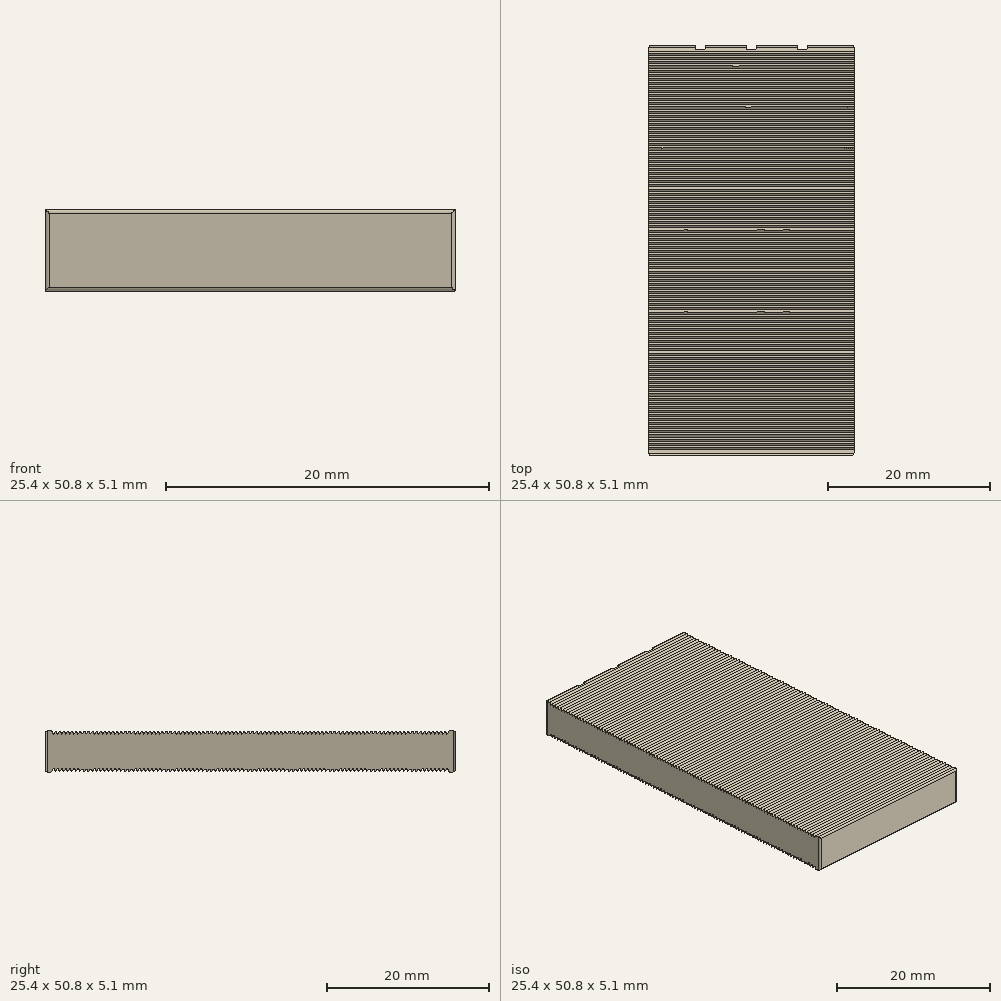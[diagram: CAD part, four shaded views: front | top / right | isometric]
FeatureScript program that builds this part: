
annotation { "Feature Type Name" : "Feature", "Feature Type Description" : "" }
export const myFeature = defineFeature(function(context is Context, id is Id, definition is map)
    precondition{}
    {
        {
            var Q0;
            Q0=qCreatedBy(makeId("Front.planeOp"),FACE);
            var sketch = newSketch(context, id + "F0", { "sketchPlane" : qUnion([Q0])});
            skLineSegment(sketch, "E0.bottom", {"start": v(12.7, -2.54) * mm, "end": v(-12.7, -2.54) * mm});
            skLineSegment(sketch, "E0.top", {"start": v(12.7, 2.54) * mm, "end": v(-12.7, 2.54) * mm});
            skLineSegment(sketch, "E0.left", {"start": v(12.7, -2.54) * mm, "end": v(12.7, 2.54) * mm});
            skLineSegment(sketch, "E0.right", {"start": v(-12.7, -2.54) * mm, "end": v(-12.7, 2.54) * mm});
            skPoint(sketch, "E0.middle", {"position": v(0, 0) * mm});
            skSolve(sketch);
        }
        {
            var Q0;
            Q0=qSketchRegion(id+"F0",true);
            extrude(context, id + "F1", {"entities" : qUnion([Q0]), "endBound" : BoundingType.SYMMETRIC, "depth" : 50.8 * mm, "offsetDistance" : 25.4 * mm});
        }
        {
            var Q0;
            Q0=qCreatedBy(makeId("Right.planeOp"),FACE);
            var sketch = newSketch(context, id + "F2", { "sketchPlane" : qUnion([Q0])});
            skLineSegment(sketch, "E1", {"start": v(0.25, -2.54) * mm, "end": v(0, -2.1) * mm});
            skLineSegment(sketch, "E2", {"start": v(0, -2.1) * mm, "end": v(-0.25, -2.54) * mm});
            skLineSegment(sketch, "E3.1.0.0", {"start": v(0.76, -2.54) * mm, "end": v(0.5, -2.1) * mm});
            skLineSegment(sketch, "E3.1.0.1", {"start": v(0.5, -2.1) * mm, "end": v(0.25, -2.54) * mm});
            skLineSegment(sketch, "E3.2.0.0", {"start": v(1.27, -2.54) * mm, "end": v(1.02, -2.1) * mm});
            skLineSegment(sketch, "E3.2.0.1", {"start": v(1.02, -2.1) * mm, "end": v(0.76, -2.54) * mm});
            skLineSegment(sketch, "E3.3.0.0", {"start": v(1.78, -2.54) * mm, "end": v(1.52, -2.1) * mm});
            skLineSegment(sketch, "E3.3.0.1", {"start": v(1.52, -2.1) * mm, "end": v(1.27, -2.54) * mm});
            skLineSegment(sketch, "E3.4.0.0", {"start": v(2.29, -2.54) * mm, "end": v(2.03, -2.1) * mm});
            skLineSegment(sketch, "E3.4.0.1", {"start": v(2.03, -2.1) * mm, "end": v(1.78, -2.54) * mm});
            skLineSegment(sketch, "E3.5.0.0", {"start": v(2.8, -2.54) * mm, "end": v(2.54, -2.1) * mm});
            skLineSegment(sketch, "E3.5.0.1", {"start": v(2.54, -2.1) * mm, "end": v(2.29, -2.54) * mm});
            skLineSegment(sketch, "E3.6.0.0", {"start": v(3.3, -2.54) * mm, "end": v(3.05, -2.1) * mm});
            skLineSegment(sketch, "E3.6.0.1", {"start": v(3.05, -2.1) * mm, "end": v(2.8, -2.54) * mm});
            skLineSegment(sketch, "E3.7.0.0", {"start": v(3.81, -2.54) * mm, "end": v(3.56, -2.1) * mm});
            skLineSegment(sketch, "E3.7.0.1", {"start": v(3.56, -2.1) * mm, "end": v(3.3, -2.54) * mm});
            skLineSegment(sketch, "E3.8.0.0", {"start": v(4.32, -2.54) * mm, "end": v(4.06, -2.1) * mm});
            skLineSegment(sketch, "E3.8.0.1", {"start": v(4.06, -2.1) * mm, "end": v(3.81, -2.54) * mm});
            skLineSegment(sketch, "E3.9.0.0", {"start": v(4.83, -2.54) * mm, "end": v(4.57, -2.1) * mm});
            skLineSegment(sketch, "E3.9.0.1", {"start": v(4.57, -2.1) * mm, "end": v(4.32, -2.54) * mm});
            skLineSegment(sketch, "E3.10.0.0", {"start": v(5.33, -2.54) * mm, "end": v(5.08, -2.1) * mm});
            skLineSegment(sketch, "E3.10.0.1", {"start": v(5.08, -2.1) * mm, "end": v(4.83, -2.54) * mm});
            skLineSegment(sketch, "E3.11.0.0", {"start": v(5.84, -2.54) * mm, "end": v(5.59, -2.1) * mm});
            skLineSegment(sketch, "E3.11.0.1", {"start": v(5.59, -2.1) * mm, "end": v(5.33, -2.54) * mm});
            skLineSegment(sketch, "E3.12.0.0", {"start": v(6.35, -2.54) * mm, "end": v(6.1, -2.1) * mm});
            skLineSegment(sketch, "E3.12.0.1", {"start": v(6.1, -2.1) * mm, "end": v(5.84, -2.54) * mm});
            skLineSegment(sketch, "E3.13.0.0", {"start": v(6.86, -2.54) * mm, "end": v(6.6, -2.1) * mm});
            skLineSegment(sketch, "E3.13.0.1", {"start": v(6.6, -2.1) * mm, "end": v(6.35, -2.54) * mm});
            skLineSegment(sketch, "E3.14.0.0", {"start": v(7.37, -2.54) * mm, "end": v(7.11, -2.1) * mm});
            skLineSegment(sketch, "E3.14.0.1", {"start": v(7.11, -2.1) * mm, "end": v(6.86, -2.54) * mm});
            skLineSegment(sketch, "E3.15.0.0", {"start": v(7.87, -2.54) * mm, "end": v(7.62, -2.1) * mm});
            skLineSegment(sketch, "E3.15.0.1", {"start": v(7.62, -2.1) * mm, "end": v(7.37, -2.54) * mm});
            skLineSegment(sketch, "E3.16.0.0", {"start": v(8.38, -2.54) * mm, "end": v(8.13, -2.1) * mm});
            skLineSegment(sketch, "E3.16.0.1", {"start": v(8.13, -2.1) * mm, "end": v(7.87, -2.54) * mm});
            skLineSegment(sketch, "E3.17.0.0", {"start": v(8.9, -2.54) * mm, "end": v(8.64, -2.1) * mm});
            skLineSegment(sketch, "E3.17.0.1", {"start": v(8.64, -2.1) * mm, "end": v(8.38, -2.54) * mm});
            skLineSegment(sketch, "E3.18.0.0", {"start": v(9.4, -2.54) * mm, "end": v(9.14, -2.1) * mm});
            skLineSegment(sketch, "E3.18.0.1", {"start": v(9.14, -2.1) * mm, "end": v(8.9, -2.54) * mm});
            skLineSegment(sketch, "E3.19.0.0", {"start": v(9.9, -2.54) * mm, "end": v(9.65, -2.1) * mm});
            skLineSegment(sketch, "E3.19.0.1", {"start": v(9.65, -2.1) * mm, "end": v(9.4, -2.54) * mm});
            skLineSegment(sketch, "E3.20.0.0", {"start": v(10.41, -2.54) * mm, "end": v(10.16, -2.1) * mm});
            skLineSegment(sketch, "E3.20.0.1", {"start": v(10.16, -2.1) * mm, "end": v(9.9, -2.54) * mm});
            skLineSegment(sketch, "E3.21.0.0", {"start": v(10.92, -2.54) * mm, "end": v(10.67, -2.1) * mm});
            skLineSegment(sketch, "E3.21.0.1", {"start": v(10.67, -2.1) * mm, "end": v(10.41, -2.54) * mm});
            skLineSegment(sketch, "E3.22.0.0", {"start": v(11.43, -2.54) * mm, "end": v(11.18, -2.1) * mm});
            skLineSegment(sketch, "E3.22.0.1", {"start": v(11.18, -2.1) * mm, "end": v(10.92, -2.54) * mm});
            skLineSegment(sketch, "E3.23.0.0", {"start": v(11.94, -2.54) * mm, "end": v(11.68, -2.1) * mm});
            skLineSegment(sketch, "E3.23.0.1", {"start": v(11.68, -2.1) * mm, "end": v(11.43, -2.54) * mm});
            skLineSegment(sketch, "E3.24.0.0", {"start": v(12.45, -2.54) * mm, "end": v(12.2, -2.1) * mm});
            skLineSegment(sketch, "E3.24.0.1", {"start": v(12.2, -2.1) * mm, "end": v(11.94, -2.54) * mm});
            skLineSegment(sketch, "E3.25.0.0", {"start": v(12.95, -2.54) * mm, "end": v(12.7, -2.1) * mm});
            skLineSegment(sketch, "E3.25.0.1", {"start": v(12.7, -2.1) * mm, "end": v(12.45, -2.54) * mm});
            skLineSegment(sketch, "E3.26.0.0", {"start": v(13.46, -2.54) * mm, "end": v(13.2, -2.1) * mm});
            skLineSegment(sketch, "E3.26.0.1", {"start": v(13.2, -2.1) * mm, "end": v(12.95, -2.54) * mm});
            skLineSegment(sketch, "E3.27.0.0", {"start": v(13.97, -2.54) * mm, "end": v(13.72, -2.1) * mm});
            skLineSegment(sketch, "E3.27.0.1", {"start": v(13.72, -2.1) * mm, "end": v(13.46, -2.54) * mm});
            skLineSegment(sketch, "E3.28.0.0", {"start": v(14.48, -2.54) * mm, "end": v(14.22, -2.1) * mm});
            skLineSegment(sketch, "E3.28.0.1", {"start": v(14.22, -2.1) * mm, "end": v(13.97, -2.54) * mm});
            skLineSegment(sketch, "E3.29.0.0", {"start": v(14.99, -2.54) * mm, "end": v(14.73, -2.1) * mm});
            skLineSegment(sketch, "E3.29.0.1", {"start": v(14.73, -2.1) * mm, "end": v(14.48, -2.54) * mm});
            skLineSegment(sketch, "E3.30.0.0", {"start": v(15.5, -2.54) * mm, "end": v(15.24, -2.1) * mm});
            skLineSegment(sketch, "E3.30.0.1", {"start": v(15.24, -2.1) * mm, "end": v(14.99, -2.54) * mm});
            skLineSegment(sketch, "E3.31.0.0", {"start": v(16, -2.54) * mm, "end": v(15.75, -2.1) * mm});
            skLineSegment(sketch, "E3.31.0.1", {"start": v(15.75, -2.1) * mm, "end": v(15.5, -2.54) * mm});
            skLineSegment(sketch, "E3.32.0.0", {"start": v(16.51, -2.54) * mm, "end": v(16.26, -2.1) * mm});
            skLineSegment(sketch, "E3.32.0.1", {"start": v(16.26, -2.1) * mm, "end": v(16, -2.54) * mm});
            skLineSegment(sketch, "E3.33.0.0", {"start": v(17.02, -2.54) * mm, "end": v(16.76, -2.1) * mm});
            skLineSegment(sketch, "E3.33.0.1", {"start": v(16.76, -2.1) * mm, "end": v(16.51, -2.54) * mm});
            skLineSegment(sketch, "E3.34.0.0", {"start": v(17.53, -2.54) * mm, "end": v(17.27, -2.1) * mm});
            skLineSegment(sketch, "E3.34.0.1", {"start": v(17.27, -2.1) * mm, "end": v(17.02, -2.54) * mm});
            skLineSegment(sketch, "E3.35.0.0", {"start": v(18.03, -2.54) * mm, "end": v(17.78, -2.1) * mm});
            skLineSegment(sketch, "E3.35.0.1", {"start": v(17.78, -2.1) * mm, "end": v(17.53, -2.54) * mm});
            skLineSegment(sketch, "E3.36.0.0", {"start": v(18.54, -2.54) * mm, "end": v(18.29, -2.1) * mm});
            skLineSegment(sketch, "E3.36.0.1", {"start": v(18.29, -2.1) * mm, "end": v(18.03, -2.54) * mm});
            skLineSegment(sketch, "E3.37.0.0", {"start": v(19.05, -2.54) * mm, "end": v(18.8, -2.1) * mm});
            skLineSegment(sketch, "E3.37.0.1", {"start": v(18.8, -2.1) * mm, "end": v(18.54, -2.54) * mm});
            skLineSegment(sketch, "E3.38.0.0", {"start": v(19.56, -2.54) * mm, "end": v(19.3, -2.1) * mm});
            skLineSegment(sketch, "E3.38.0.1", {"start": v(19.3, -2.1) * mm, "end": v(19.05, -2.54) * mm});
            skLineSegment(sketch, "E3.39.0.0", {"start": v(20.07, -2.54) * mm, "end": v(19.81, -2.1) * mm});
            skLineSegment(sketch, "E3.39.0.1", {"start": v(19.81, -2.1) * mm, "end": v(19.56, -2.54) * mm});
            skLineSegment(sketch, "E3.40.0.0", {"start": v(20.57, -2.54) * mm, "end": v(20.32, -2.1) * mm});
            skLineSegment(sketch, "E3.40.0.1", {"start": v(20.32, -2.1) * mm, "end": v(20.07, -2.54) * mm});
            skLineSegment(sketch, "E3.41.0.0", {"start": v(21.08, -2.54) * mm, "end": v(20.83, -2.1) * mm});
            skLineSegment(sketch, "E3.41.0.1", {"start": v(20.83, -2.1) * mm, "end": v(20.57, -2.54) * mm});
            skLineSegment(sketch, "E3.42.0.0", {"start": v(21.6, -2.54) * mm, "end": v(21.34, -2.1) * mm});
            skLineSegment(sketch, "E3.42.0.1", {"start": v(21.34, -2.1) * mm, "end": v(21.08, -2.54) * mm});
            skLineSegment(sketch, "E3.43.0.0", {"start": v(22.1, -2.54) * mm, "end": v(21.84, -2.1) * mm});
            skLineSegment(sketch, "E3.43.0.1", {"start": v(21.84, -2.1) * mm, "end": v(21.6, -2.54) * mm});
            skLineSegment(sketch, "E3.44.0.0", {"start": v(22.6, -2.54) * mm, "end": v(22.35, -2.1) * mm});
            skLineSegment(sketch, "E3.44.0.1", {"start": v(22.35, -2.1) * mm, "end": v(22.1, -2.54) * mm});
            skLineSegment(sketch, "E3.45.0.0", {"start": v(23.11, -2.54) * mm, "end": v(22.86, -2.1) * mm});
            skLineSegment(sketch, "E3.45.0.1", {"start": v(22.86, -2.1) * mm, "end": v(22.6, -2.54) * mm});
            skLineSegment(sketch, "E3.46.0.0", {"start": v(23.62, -2.54) * mm, "end": v(23.37, -2.1) * mm});
            skLineSegment(sketch, "E3.46.0.1", {"start": v(23.37, -2.1) * mm, "end": v(23.11, -2.54) * mm});
            skLineSegment(sketch, "E3.47.0.0", {"start": v(24.13, -2.54) * mm, "end": v(23.88, -2.1) * mm});
            skLineSegment(sketch, "E3.47.0.1", {"start": v(23.88, -2.1) * mm, "end": v(23.62, -2.54) * mm});
            skLineSegment(sketch, "E3.48.0.0", {"start": v(24.64, -2.54) * mm, "end": v(24.38, -2.1) * mm});
            skLineSegment(sketch, "E3.48.0.1", {"start": v(24.38, -2.1) * mm, "end": v(24.13, -2.54) * mm});
            skLineSegment(sketch, "E3.direction1", {"start": v(-0.25, -2.54) * mm, "end": v(0.25, -2.54) * mm, "construction": true});
            skLineSegment(sketch, "E4.1.0.0", {"start": v(-0.25, -2.54) * mm, "end": v(-0.5, -2.1) * mm});
            skLineSegment(sketch, "E4.1.0.1", {"start": v(-0.5, -2.1) * mm, "end": v(-0.76, -2.54) * mm});
            skLineSegment(sketch, "E4.2.0.0", {"start": v(-0.76, -2.54) * mm, "end": v(-1.02, -2.1) * mm});
            skLineSegment(sketch, "E4.2.0.1", {"start": v(-1.02, -2.1) * mm, "end": v(-1.27, -2.54) * mm});
            skLineSegment(sketch, "E4.3.0.0", {"start": v(-1.27, -2.54) * mm, "end": v(-1.52, -2.1) * mm});
            skLineSegment(sketch, "E4.3.0.1", {"start": v(-1.52, -2.1) * mm, "end": v(-1.78, -2.54) * mm});
            skLineSegment(sketch, "E4.4.0.0", {"start": v(-1.78, -2.54) * mm, "end": v(-2.03, -2.1) * mm});
            skLineSegment(sketch, "E4.4.0.1", {"start": v(-2.03, -2.1) * mm, "end": v(-2.29, -2.54) * mm});
            skLineSegment(sketch, "E4.5.0.0", {"start": v(-2.29, -2.54) * mm, "end": v(-2.54, -2.1) * mm});
            skLineSegment(sketch, "E4.5.0.1", {"start": v(-2.54, -2.1) * mm, "end": v(-2.8, -2.54) * mm});
            skLineSegment(sketch, "E4.6.0.0", {"start": v(-2.8, -2.54) * mm, "end": v(-3.05, -2.1) * mm});
            skLineSegment(sketch, "E4.6.0.1", {"start": v(-3.05, -2.1) * mm, "end": v(-3.3, -2.54) * mm});
            skLineSegment(sketch, "E4.7.0.0", {"start": v(-3.3, -2.54) * mm, "end": v(-3.56, -2.1) * mm});
            skLineSegment(sketch, "E4.7.0.1", {"start": v(-3.56, -2.1) * mm, "end": v(-3.8, -2.54) * mm});
            skLineSegment(sketch, "E4.8.0.0", {"start": v(-3.8, -2.54) * mm, "end": v(-4.06, -2.1) * mm});
            skLineSegment(sketch, "E4.8.0.1", {"start": v(-4.06, -2.1) * mm, "end": v(-4.32, -2.54) * mm});
            skLineSegment(sketch, "E4.9.0.0", {"start": v(-4.32, -2.54) * mm, "end": v(-4.57, -2.1) * mm});
            skLineSegment(sketch, "E4.9.0.1", {"start": v(-4.57, -2.1) * mm, "end": v(-4.83, -2.54) * mm});
            skLineSegment(sketch, "E4.10.0.0", {"start": v(-4.83, -2.54) * mm, "end": v(-5.08, -2.1) * mm});
            skLineSegment(sketch, "E4.10.0.1", {"start": v(-5.08, -2.1) * mm, "end": v(-5.33, -2.54) * mm});
            skLineSegment(sketch, "E4.11.0.0", {"start": v(-5.33, -2.54) * mm, "end": v(-5.59, -2.1) * mm});
            skLineSegment(sketch, "E4.11.0.1", {"start": v(-5.59, -2.1) * mm, "end": v(-5.84, -2.54) * mm});
            skLineSegment(sketch, "E4.12.0.0", {"start": v(-5.84, -2.54) * mm, "end": v(-6.1, -2.1) * mm});
            skLineSegment(sketch, "E4.12.0.1", {"start": v(-6.1, -2.1) * mm, "end": v(-6.35, -2.54) * mm});
            skLineSegment(sketch, "E4.13.0.0", {"start": v(-6.35, -2.54) * mm, "end": v(-6.6, -2.1) * mm});
            skLineSegment(sketch, "E4.13.0.1", {"start": v(-6.6, -2.1) * mm, "end": v(-6.86, -2.54) * mm});
            skLineSegment(sketch, "E4.14.0.0", {"start": v(-6.86, -2.54) * mm, "end": v(-7.11, -2.1) * mm});
            skLineSegment(sketch, "E4.14.0.1", {"start": v(-7.11, -2.1) * mm, "end": v(-7.37, -2.54) * mm});
            skLineSegment(sketch, "E4.15.0.0", {"start": v(-7.37, -2.54) * mm, "end": v(-7.62, -2.1) * mm});
            skLineSegment(sketch, "E4.15.0.1", {"start": v(-7.62, -2.1) * mm, "end": v(-7.87, -2.54) * mm});
            skLineSegment(sketch, "E4.16.0.0", {"start": v(-7.87, -2.54) * mm, "end": v(-8.13, -2.1) * mm});
            skLineSegment(sketch, "E4.16.0.1", {"start": v(-8.13, -2.1) * mm, "end": v(-8.38, -2.54) * mm});
            skLineSegment(sketch, "E4.17.0.0", {"start": v(-8.38, -2.54) * mm, "end": v(-8.64, -2.1) * mm});
            skLineSegment(sketch, "E4.17.0.1", {"start": v(-8.64, -2.1) * mm, "end": v(-8.89, -2.54) * mm});
            skLineSegment(sketch, "E4.18.0.0", {"start": v(-8.89, -2.54) * mm, "end": v(-9.14, -2.1) * mm});
            skLineSegment(sketch, "E4.18.0.1", {"start": v(-9.14, -2.1) * mm, "end": v(-9.4, -2.54) * mm});
            skLineSegment(sketch, "E4.19.0.0", {"start": v(-9.4, -2.54) * mm, "end": v(-9.65, -2.1) * mm});
            skLineSegment(sketch, "E4.19.0.1", {"start": v(-9.65, -2.1) * mm, "end": v(-9.9, -2.54) * mm});
            skLineSegment(sketch, "E4.20.0.0", {"start": v(-9.9, -2.54) * mm, "end": v(-10.16, -2.1) * mm});
            skLineSegment(sketch, "E4.20.0.1", {"start": v(-10.16, -2.1) * mm, "end": v(-10.41, -2.54) * mm});
            skLineSegment(sketch, "E4.21.0.0", {"start": v(-10.41, -2.54) * mm, "end": v(-10.67, -2.1) * mm});
            skLineSegment(sketch, "E4.21.0.1", {"start": v(-10.67, -2.1) * mm, "end": v(-10.92, -2.54) * mm});
            skLineSegment(sketch, "E4.22.0.0", {"start": v(-10.92, -2.54) * mm, "end": v(-11.18, -2.1) * mm});
            skLineSegment(sketch, "E4.22.0.1", {"start": v(-11.18, -2.1) * mm, "end": v(-11.43, -2.54) * mm});
            skLineSegment(sketch, "E4.23.0.0", {"start": v(-11.43, -2.54) * mm, "end": v(-11.68, -2.1) * mm});
            skLineSegment(sketch, "E4.23.0.1", {"start": v(-11.68, -2.1) * mm, "end": v(-11.94, -2.54) * mm});
            skLineSegment(sketch, "E4.24.0.0", {"start": v(-11.94, -2.54) * mm, "end": v(-12.2, -2.1) * mm});
            skLineSegment(sketch, "E4.24.0.1", {"start": v(-12.2, -2.1) * mm, "end": v(-12.45, -2.54) * mm});
            skLineSegment(sketch, "E4.25.0.0", {"start": v(-12.45, -2.54) * mm, "end": v(-12.7, -2.1) * mm});
            skLineSegment(sketch, "E4.25.0.1", {"start": v(-12.7, -2.1) * mm, "end": v(-12.95, -2.54) * mm});
            skLineSegment(sketch, "E4.26.0.0", {"start": v(-12.95, -2.54) * mm, "end": v(-13.2, -2.1) * mm});
            skLineSegment(sketch, "E4.26.0.1", {"start": v(-13.2, -2.1) * mm, "end": v(-13.46, -2.54) * mm});
            skLineSegment(sketch, "E4.27.0.0", {"start": v(-13.46, -2.54) * mm, "end": v(-13.72, -2.1) * mm});
            skLineSegment(sketch, "E4.27.0.1", {"start": v(-13.72, -2.1) * mm, "end": v(-13.97, -2.54) * mm});
            skLineSegment(sketch, "E4.28.0.0", {"start": v(-13.97, -2.54) * mm, "end": v(-14.22, -2.1) * mm});
            skLineSegment(sketch, "E4.28.0.1", {"start": v(-14.22, -2.1) * mm, "end": v(-14.48, -2.54) * mm});
            skLineSegment(sketch, "E4.29.0.0", {"start": v(-14.48, -2.54) * mm, "end": v(-14.73, -2.1) * mm});
            skLineSegment(sketch, "E4.29.0.1", {"start": v(-14.73, -2.1) * mm, "end": v(-14.99, -2.54) * mm});
            skLineSegment(sketch, "E4.30.0.0", {"start": v(-14.99, -2.54) * mm, "end": v(-15.24, -2.1) * mm});
            skLineSegment(sketch, "E4.30.0.1", {"start": v(-15.24, -2.1) * mm, "end": v(-15.5, -2.54) * mm});
            skLineSegment(sketch, "E4.31.0.0", {"start": v(-15.5, -2.54) * mm, "end": v(-15.75, -2.1) * mm});
            skLineSegment(sketch, "E4.31.0.1", {"start": v(-15.75, -2.1) * mm, "end": v(-16, -2.54) * mm});
            skLineSegment(sketch, "E4.32.0.0", {"start": v(-16, -2.54) * mm, "end": v(-16.26, -2.1) * mm});
            skLineSegment(sketch, "E4.32.0.1", {"start": v(-16.26, -2.1) * mm, "end": v(-16.5, -2.54) * mm});
            skLineSegment(sketch, "E4.33.0.0", {"start": v(-16.5, -2.54) * mm, "end": v(-16.76, -2.1) * mm});
            skLineSegment(sketch, "E4.33.0.1", {"start": v(-16.76, -2.1) * mm, "end": v(-17.02, -2.54) * mm});
            skLineSegment(sketch, "E4.34.0.0", {"start": v(-17.02, -2.54) * mm, "end": v(-17.27, -2.1) * mm});
            skLineSegment(sketch, "E4.34.0.1", {"start": v(-17.27, -2.1) * mm, "end": v(-17.53, -2.54) * mm});
            skLineSegment(sketch, "E4.35.0.0", {"start": v(-17.53, -2.54) * mm, "end": v(-17.78, -2.1) * mm});
            skLineSegment(sketch, "E4.35.0.1", {"start": v(-17.78, -2.1) * mm, "end": v(-18.03, -2.54) * mm});
            skLineSegment(sketch, "E4.36.0.0", {"start": v(-18.03, -2.54) * mm, "end": v(-18.29, -2.1) * mm});
            skLineSegment(sketch, "E4.36.0.1", {"start": v(-18.29, -2.1) * mm, "end": v(-18.54, -2.54) * mm});
            skLineSegment(sketch, "E4.37.0.0", {"start": v(-18.54, -2.54) * mm, "end": v(-18.8, -2.1) * mm});
            skLineSegment(sketch, "E4.37.0.1", {"start": v(-18.8, -2.1) * mm, "end": v(-19.05, -2.54) * mm});
            skLineSegment(sketch, "E4.38.0.0", {"start": v(-19.05, -2.54) * mm, "end": v(-19.3, -2.1) * mm});
            skLineSegment(sketch, "E4.38.0.1", {"start": v(-19.3, -2.1) * mm, "end": v(-19.56, -2.54) * mm});
            skLineSegment(sketch, "E4.39.0.0", {"start": v(-19.56, -2.54) * mm, "end": v(-19.81, -2.1) * mm});
            skLineSegment(sketch, "E4.39.0.1", {"start": v(-19.81, -2.1) * mm, "end": v(-20.07, -2.54) * mm});
            skLineSegment(sketch, "E4.40.0.0", {"start": v(-20.07, -2.54) * mm, "end": v(-20.32, -2.1) * mm});
            skLineSegment(sketch, "E4.40.0.1", {"start": v(-20.32, -2.1) * mm, "end": v(-20.57, -2.54) * mm});
            skLineSegment(sketch, "E4.41.0.0", {"start": v(-20.57, -2.54) * mm, "end": v(-20.83, -2.1) * mm});
            skLineSegment(sketch, "E4.41.0.1", {"start": v(-20.83, -2.1) * mm, "end": v(-21.08, -2.54) * mm});
            skLineSegment(sketch, "E4.42.0.0", {"start": v(-21.08, -2.54) * mm, "end": v(-21.34, -2.1) * mm});
            skLineSegment(sketch, "E4.42.0.1", {"start": v(-21.34, -2.1) * mm, "end": v(-21.59, -2.54) * mm});
            skLineSegment(sketch, "E4.43.0.0", {"start": v(-21.59, -2.54) * mm, "end": v(-21.84, -2.1) * mm});
            skLineSegment(sketch, "E4.43.0.1", {"start": v(-21.84, -2.1) * mm, "end": v(-22.1, -2.54) * mm});
            skLineSegment(sketch, "E4.44.0.0", {"start": v(-22.1, -2.54) * mm, "end": v(-22.35, -2.1) * mm});
            skLineSegment(sketch, "E4.44.0.1", {"start": v(-22.35, -2.1) * mm, "end": v(-22.6, -2.54) * mm});
            skLineSegment(sketch, "E4.45.0.0", {"start": v(-22.6, -2.54) * mm, "end": v(-22.86, -2.1) * mm});
            skLineSegment(sketch, "E4.45.0.1", {"start": v(-22.86, -2.1) * mm, "end": v(-23.11, -2.54) * mm});
            skLineSegment(sketch, "E4.46.0.0", {"start": v(-23.11, -2.54) * mm, "end": v(-23.37, -2.1) * mm});
            skLineSegment(sketch, "E4.46.0.1", {"start": v(-23.37, -2.1) * mm, "end": v(-23.62, -2.54) * mm});
            skLineSegment(sketch, "E4.47.0.0", {"start": v(-23.62, -2.54) * mm, "end": v(-23.88, -2.1) * mm});
            skLineSegment(sketch, "E4.47.0.1", {"start": v(-23.88, -2.1) * mm, "end": v(-24.13, -2.54) * mm});
            skLineSegment(sketch, "E4.48.0.0", {"start": v(-24.13, -2.54) * mm, "end": v(-24.38, -2.1) * mm});
            skLineSegment(sketch, "E4.48.0.1", {"start": v(-24.38, -2.1) * mm, "end": v(-24.64, -2.54) * mm});
            skLineSegment(sketch, "E4.direction1", {"start": v(-0.25, -2.54) * mm, "end": v(-0.76, -2.54) * mm, "construction": true});
            skLineSegment(sketch, "E5", {"start": v(-24.64, -2.54) * mm, "end": v(-24.64, -2.8) * mm});
            skLineSegment(sketch, "E6", {"start": v(-24.64, -2.8) * mm, "end": v(24.64, -2.8) * mm});
            skLineSegment(sketch, "E7", {"start": v(24.64, -2.8) * mm, "end": v(24.64, -2.54) * mm});
            skLineSegment(sketch, "E8.MirrorCS", {"start": v(-0.76, 2.54) * mm, "end": v(-1.02, 2.1) * mm});
            skLineSegment(sketch, "E9.MirrorCS", {"start": v(0.5, 2.1) * mm, "end": v(0.25, 2.54) * mm});
            skLineSegment(sketch, "E10.MirrorCS", {"start": v(-0.25, 2.54) * mm, "end": v(-0.5, 2.1) * mm});
            skLineSegment(sketch, "E11.MirrorCS", {"start": v(13.2, 2.1) * mm, "end": v(12.95, 2.54) * mm});
            skLineSegment(sketch, "E12.MirrorCS", {"start": v(-0.25, 2.54) * mm, "end": v(0.25, 2.54) * mm, "construction": true});
            skLineSegment(sketch, "E13.MirrorCS", {"start": v(-0.25, 2.54) * mm, "end": v(-0.76, 2.54) * mm, "construction": true});
            skLineSegment(sketch, "E14.MirrorCS", {"start": v(13.46, 2.54) * mm, "end": v(13.2, 2.1) * mm});
            skLineSegment(sketch, "E15.MirrorCS", {"start": v(-1.02, 2.1) * mm, "end": v(-1.27, 2.54) * mm});
            skLineSegment(sketch, "E16.MirrorCS", {"start": v(21.6, 2.54) * mm, "end": v(21.34, 2.1) * mm});
            skLineSegment(sketch, "E17.MirrorCS", {"start": v(-0.5, 2.1) * mm, "end": v(-0.76, 2.54) * mm});
            skLineSegment(sketch, "E18.MirrorCS", {"start": v(0, 2.1) * mm, "end": v(-0.25, 2.54) * mm});
            skLineSegment(sketch, "E19.MirrorCS", {"start": v(0.25, 2.54) * mm, "end": v(0, 2.1) * mm});
            skLineSegment(sketch, "E20.MirrorCS", {"start": v(21.34, 2.1) * mm, "end": v(21.08, 2.54) * mm});
            skLineSegment(sketch, "E21.MirrorCS", {"start": v(-12.7, 2.1) * mm, "end": v(-12.95, 2.54) * mm});
            skLineSegment(sketch, "E22.MirrorCS", {"start": v(12.95, 2.54) * mm, "end": v(12.7, 2.1) * mm});
            skLineSegment(sketch, "E23.MirrorCS", {"start": v(7.87, 2.54) * mm, "end": v(7.62, 2.1) * mm});
            skLineSegment(sketch, "E24.MirrorCS", {"start": v(-2.54, 2.1) * mm, "end": v(-2.8, 2.54) * mm});
            skLineSegment(sketch, "E25.MirrorCS", {"start": v(-20.83, 2.1) * mm, "end": v(-21.08, 2.54) * mm});
            skLineSegment(sketch, "E26.MirrorCS", {"start": v(22.6, 2.54) * mm, "end": v(22.35, 2.1) * mm});
            skLineSegment(sketch, "E27.MirrorCS", {"start": v(-8.89, 2.54) * mm, "end": v(-9.14, 2.1) * mm});
            skLineSegment(sketch, "E28.MirrorCS", {"start": v(-22.6, 2.54) * mm, "end": v(-22.86, 2.1) * mm});
            skLineSegment(sketch, "E29.MirrorCS", {"start": v(-17.02, 2.54) * mm, "end": v(-17.27, 2.1) * mm});
            skLineSegment(sketch, "E30.MirrorCS", {"start": v(-6.35, 2.54) * mm, "end": v(-6.6, 2.1) * mm});
            skLineSegment(sketch, "E31.MirrorCS", {"start": v(9.4, 2.54) * mm, "end": v(9.14, 2.1) * mm});
            skLineSegment(sketch, "E32.MirrorCS", {"start": v(-4.57, 2.1) * mm, "end": v(-4.83, 2.54) * mm});
            skLineSegment(sketch, "E33.MirrorCS", {"start": v(-21.08, 2.54) * mm, "end": v(-21.34, 2.1) * mm});
            skLineSegment(sketch, "E34.MirrorCS", {"start": v(23.11, 2.54) * mm, "end": v(22.86, 2.1) * mm});
            skLineSegment(sketch, "E35.MirrorCS", {"start": v(4.06, 2.1) * mm, "end": v(3.81, 2.54) * mm});
            skLineSegment(sketch, "E36.MirrorCS", {"start": v(-12.95, 2.54) * mm, "end": v(-13.2, 2.1) * mm});
            skLineSegment(sketch, "E37.MirrorCS", {"start": v(-23.11, 2.54) * mm, "end": v(-23.37, 2.1) * mm});
            skLineSegment(sketch, "E38.MirrorCS", {"start": v(-1.27, 2.54) * mm, "end": v(-1.52, 2.1) * mm});
            skLineSegment(sketch, "E39.MirrorCS", {"start": v(-7.62, 2.1) * mm, "end": v(-7.87, 2.54) * mm});
            skLineSegment(sketch, "E40.MirrorCS", {"start": v(-7.87, 2.54) * mm, "end": v(-8.13, 2.1) * mm});
            skLineSegment(sketch, "E41.MirrorCS", {"start": v(-16.5, 2.54) * mm, "end": v(-16.76, 2.1) * mm});
            skLineSegment(sketch, "E42.MirrorCS", {"start": v(-2.8, 2.54) * mm, "end": v(-3.05, 2.1) * mm});
            skLineSegment(sketch, "E43.MirrorCS", {"start": v(-16, 2.54) * mm, "end": v(-16.26, 2.1) * mm});
            skLineSegment(sketch, "E44.MirrorCS", {"start": v(21.08, 2.54) * mm, "end": v(20.83, 2.1) * mm});
            skLineSegment(sketch, "E45.MirrorCS", {"start": v(-14.99, 2.54) * mm, "end": v(-15.24, 2.1) * mm});
            skLineSegment(sketch, "E46.MirrorCS", {"start": v(-3.8, 2.54) * mm, "end": v(-4.06, 2.1) * mm});
            skLineSegment(sketch, "E47.MirrorCS", {"start": v(-2.29, 2.54) * mm, "end": v(-2.54, 2.1) * mm});
            skLineSegment(sketch, "E48.MirrorCS", {"start": v(-13.2, 2.1) * mm, "end": v(-13.46, 2.54) * mm});
            skLineSegment(sketch, "E49.MirrorCS", {"start": v(6.35, 2.54) * mm, "end": v(6.1, 2.1) * mm});
            skLineSegment(sketch, "E50.MirrorCS", {"start": v(-8.64, 2.1) * mm, "end": v(-8.89, 2.54) * mm});
            skLineSegment(sketch, "E51.MirrorCS", {"start": v(-8.38, 2.54) * mm, "end": v(-8.64, 2.1) * mm});
            skLineSegment(sketch, "E52.MirrorCS", {"start": v(14.73, 2.1) * mm, "end": v(14.48, 2.54) * mm});
            skLineSegment(sketch, "E53.MirrorCS", {"start": v(-4.83, 2.54) * mm, "end": v(-5.08, 2.1) * mm});
            skLineSegment(sketch, "E54.MirrorCS", {"start": v(3.56, 2.1) * mm, "end": v(3.3, 2.54) * mm});
            skLineSegment(sketch, "E55.MirrorCS", {"start": v(-16.76, 2.1) * mm, "end": v(-17.02, 2.54) * mm});
            skLineSegment(sketch, "E56.MirrorCS", {"start": v(6.6, 2.1) * mm, "end": v(6.35, 2.54) * mm});
            skLineSegment(sketch, "E57.MirrorCS", {"start": v(-4.06, 2.1) * mm, "end": v(-4.32, 2.54) * mm});
            skLineSegment(sketch, "E58.MirrorCS", {"start": v(1.27, 2.54) * mm, "end": v(1.02, 2.1) * mm});
            skLineSegment(sketch, "E59.MirrorCS", {"start": v(14.48, 2.54) * mm, "end": v(14.22, 2.1) * mm});
            skLineSegment(sketch, "E60.MirrorCS", {"start": v(-15.24, 2.1) * mm, "end": v(-15.5, 2.54) * mm});
            skLineSegment(sketch, "E61.MirrorCS", {"start": v(-14.73, 2.1) * mm, "end": v(-14.99, 2.54) * mm});
            skLineSegment(sketch, "E62.MirrorCS", {"start": v(-3.56, 2.1) * mm, "end": v(-3.8, 2.54) * mm});
            skLineSegment(sketch, "E63.MirrorCS", {"start": v(1.02, 2.1) * mm, "end": v(0.76, 2.54) * mm});
            skLineSegment(sketch, "E64.MirrorCS", {"start": v(-21.34, 2.1) * mm, "end": v(-21.59, 2.54) * mm});
            skLineSegment(sketch, "E65.MirrorCS", {"start": v(22.86, 2.1) * mm, "end": v(22.6, 2.54) * mm});
            skLineSegment(sketch, "E66.MirrorCS", {"start": v(0.76, 2.54) * mm, "end": v(0.5, 2.1) * mm});
            skLineSegment(sketch, "E67.MirrorCS", {"start": v(-19.05, 2.54) * mm, "end": v(-19.3, 2.1) * mm});
            skLineSegment(sketch, "E68.MirrorCS", {"start": v(-14.48, 2.54) * mm, "end": v(-14.73, 2.1) * mm});
            skLineSegment(sketch, "E69.MirrorCS", {"start": v(14.99, 2.54) * mm, "end": v(14.73, 2.1) * mm});
            skLineSegment(sketch, "E70.MirrorCS", {"start": v(15.5, 2.54) * mm, "end": v(15.24, 2.1) * mm});
            skLineSegment(sketch, "E71.MirrorCS", {"start": v(23.37, 2.1) * mm, "end": v(23.11, 2.54) * mm});
            skLineSegment(sketch, "E72.MirrorCS", {"start": v(-21.59, 2.54) * mm, "end": v(-21.84, 2.1) * mm});
            skLineSegment(sketch, "E73.MirrorCS", {"start": v(-10.92, 2.54) * mm, "end": v(-11.18, 2.1) * mm});
            skLineSegment(sketch, "E74.MirrorCS", {"start": v(-13.46, 2.54) * mm, "end": v(-13.72, 2.1) * mm});
            skLineSegment(sketch, "E75.MirrorCS", {"start": v(4.32, 2.54) * mm, "end": v(4.06, 2.1) * mm});
            skLineSegment(sketch, "E76.MirrorCS", {"start": v(7.11, 2.1) * mm, "end": v(6.86, 2.54) * mm});
            skLineSegment(sketch, "E77.MirrorCS", {"start": v(-22.86, 2.1) * mm, "end": v(-23.11, 2.54) * mm});
            skLineSegment(sketch, "E78.MirrorCS", {"start": v(7.37, 2.54) * mm, "end": v(7.11, 2.1) * mm});
            skLineSegment(sketch, "E79.MirrorCS", {"start": v(15.24, 2.1) * mm, "end": v(14.99, 2.54) * mm});
            skLineSegment(sketch, "E80.MirrorCS", {"start": v(15.75, 2.1) * mm, "end": v(15.5, 2.54) * mm});
            skLineSegment(sketch, "E81.MirrorCS", {"start": v(18.8, 2.1) * mm, "end": v(18.54, 2.54) * mm});
            skLineSegment(sketch, "E82.MirrorCS", {"start": v(-6.6, 2.1) * mm, "end": v(-6.86, 2.54) * mm});
            skLineSegment(sketch, "E83.MirrorCS", {"start": v(-24.64, 2.54) * mm, "end": v(-24.64, 2.8) * mm});
            skLineSegment(sketch, "E84.MirrorCS", {"start": v(-2.03, 2.1) * mm, "end": v(-2.29, 2.54) * mm});
            skLineSegment(sketch, "E85.MirrorCS", {"start": v(-9.9, 2.54) * mm, "end": v(-10.16, 2.1) * mm});
            skLineSegment(sketch, "E86.MirrorCS", {"start": v(17.27, 2.1) * mm, "end": v(17.02, 2.54) * mm});
            skLineSegment(sketch, "E87.MirrorCS", {"start": v(-24.38, 2.1) * mm, "end": v(-24.64, 2.54) * mm});
            skLineSegment(sketch, "E88.MirrorCS", {"start": v(-5.33, 2.54) * mm, "end": v(-5.59, 2.1) * mm});
            skLineSegment(sketch, "E89.MirrorCS", {"start": v(-9.14, 2.1) * mm, "end": v(-9.4, 2.54) * mm});
            skLineSegment(sketch, "E90.MirrorCS", {"start": v(-15.5, 2.54) * mm, "end": v(-15.75, 2.1) * mm});
            skLineSegment(sketch, "E91.MirrorCS", {"start": v(2.54, 2.1) * mm, "end": v(2.29, 2.54) * mm});
            skLineSegment(sketch, "E92.MirrorCS", {"start": v(-19.56, 2.54) * mm, "end": v(-19.81, 2.1) * mm});
            skLineSegment(sketch, "E93.MirrorCS", {"start": v(-20.07, 2.54) * mm, "end": v(-20.32, 2.1) * mm});
            skLineSegment(sketch, "E94.MirrorCS", {"start": v(-1.78, 2.54) * mm, "end": v(-2.03, 2.1) * mm});
            skLineSegment(sketch, "E95.MirrorCS", {"start": v(10.16, 2.1) * mm, "end": v(9.9, 2.54) * mm});
            skLineSegment(sketch, "E96.MirrorCS", {"start": v(9.9, 2.54) * mm, "end": v(9.65, 2.1) * mm});
            skLineSegment(sketch, "E97.MirrorCS", {"start": v(10.41, 2.54) * mm, "end": v(10.16, 2.1) * mm});
            skLineSegment(sketch, "E98.MirrorCS", {"start": v(17.53, 2.54) * mm, "end": v(17.27, 2.1) * mm});
            skLineSegment(sketch, "E99.MirrorCS", {"start": v(5.08, 2.1) * mm, "end": v(4.83, 2.54) * mm});
            skLineSegment(sketch, "E100.MirrorCS", {"start": v(-9.65, 2.1) * mm, "end": v(-9.9, 2.54) * mm});
            skLineSegment(sketch, "E101.MirrorCS", {"start": v(20.32, 2.1) * mm, "end": v(20.07, 2.54) * mm});
            skLineSegment(sketch, "E102.MirrorCS", {"start": v(8.13, 2.1) * mm, "end": v(7.87, 2.54) * mm});
            skLineSegment(sketch, "E103.MirrorCS", {"start": v(-8.13, 2.1) * mm, "end": v(-8.38, 2.54) * mm});
            skLineSegment(sketch, "E104.MirrorCS", {"start": v(-19.3, 2.1) * mm, "end": v(-19.56, 2.54) * mm});
            skLineSegment(sketch, "E105.MirrorCS", {"start": v(-12.45, 2.54) * mm, "end": v(-12.7, 2.1) * mm});
            skLineSegment(sketch, "E106.MirrorCS", {"start": v(-19.81, 2.1) * mm, "end": v(-20.07, 2.54) * mm});
            skLineSegment(sketch, "E107.MirrorCS", {"start": v(9.65, 2.1) * mm, "end": v(9.4, 2.54) * mm});
            skLineSegment(sketch, "E108.MirrorCS", {"start": v(-18.03, 2.54) * mm, "end": v(-18.29, 2.1) * mm});
            skLineSegment(sketch, "E109.MirrorCS", {"start": v(22.1, 2.54) * mm, "end": v(21.84, 2.1) * mm});
            skLineSegment(sketch, "E110.MirrorCS", {"start": v(18.03, 2.54) * mm, "end": v(17.78, 2.1) * mm});
            skLineSegment(sketch, "E111.MirrorCS", {"start": v(-20.57, 2.54) * mm, "end": v(-20.83, 2.1) * mm});
            skLineSegment(sketch, "E112.MirrorCS", {"start": v(-14.22, 2.1) * mm, "end": v(-14.48, 2.54) * mm});
            skLineSegment(sketch, "E113.MirrorCS", {"start": v(1.52, 2.1) * mm, "end": v(1.27, 2.54) * mm});
            skLineSegment(sketch, "E114.MirrorCS", {"start": v(13.72, 2.1) * mm, "end": v(13.46, 2.54) * mm});
            skLineSegment(sketch, "E115.MirrorCS", {"start": v(24.64, 2.8) * mm, "end": v(24.64, 2.54) * mm});
            skLineSegment(sketch, "E116.MirrorCS", {"start": v(-12.2, 2.1) * mm, "end": v(-12.45, 2.54) * mm});
            skLineSegment(sketch, "E117.MirrorCS", {"start": v(17.02, 2.54) * mm, "end": v(16.76, 2.1) * mm});
            skLineSegment(sketch, "E118.MirrorCS", {"start": v(2.03, 2.1) * mm, "end": v(1.78, 2.54) * mm});
            skLineSegment(sketch, "E119.MirrorCS", {"start": v(-18.54, 2.54) * mm, "end": v(-18.8, 2.1) * mm});
            skLineSegment(sketch, "E120.MirrorCS", {"start": v(-6.1, 2.1) * mm, "end": v(-6.35, 2.54) * mm});
            skLineSegment(sketch, "E121.MirrorCS", {"start": v(12.45, 2.54) * mm, "end": v(12.2, 2.1) * mm});
            skLineSegment(sketch, "E122.MirrorCS", {"start": v(2.29, 2.54) * mm, "end": v(2.03, 2.1) * mm});
            skLineSegment(sketch, "E123.MirrorCS", {"start": v(12.7, 2.1) * mm, "end": v(12.45, 2.54) * mm});
            skLineSegment(sketch, "E124.MirrorCS", {"start": v(-17.78, 2.1) * mm, "end": v(-18.03, 2.54) * mm});
            skLineSegment(sketch, "E125.MirrorCS", {"start": v(11.43, 2.54) * mm, "end": v(11.18, 2.1) * mm});
            skLineSegment(sketch, "E126.MirrorCS", {"start": v(-5.84, 2.54) * mm, "end": v(-6.1, 2.1) * mm});
            skLineSegment(sketch, "E127.MirrorCS", {"start": v(-22.35, 2.1) * mm, "end": v(-22.6, 2.54) * mm});
            skLineSegment(sketch, "E128.MirrorCS", {"start": v(-11.94, 2.54) * mm, "end": v(-12.2, 2.1) * mm});
            skLineSegment(sketch, "E129.MirrorCS", {"start": v(-10.41, 2.54) * mm, "end": v(-10.67, 2.1) * mm});
            skLineSegment(sketch, "E130.MirrorCS", {"start": v(-23.37, 2.1) * mm, "end": v(-23.62, 2.54) * mm});
            skLineSegment(sketch, "E131.MirrorCS", {"start": v(3.3, 2.54) * mm, "end": v(3.05, 2.1) * mm});
            skLineSegment(sketch, "E132.MirrorCS", {"start": v(10.67, 2.1) * mm, "end": v(10.41, 2.54) * mm});
            skLineSegment(sketch, "E133.MirrorCS", {"start": v(-11.68, 2.1) * mm, "end": v(-11.94, 2.54) * mm});
            skLineSegment(sketch, "E134.MirrorCS", {"start": v(20.07, 2.54) * mm, "end": v(19.81, 2.1) * mm});
            skLineSegment(sketch, "E135.MirrorCS", {"start": v(7.62, 2.1) * mm, "end": v(7.37, 2.54) * mm});
            skLineSegment(sketch, "E136.MirrorCS", {"start": v(-20.32, 2.1) * mm, "end": v(-20.57, 2.54) * mm});
            skLineSegment(sketch, "E137.MirrorCS", {"start": v(-13.72, 2.1) * mm, "end": v(-13.97, 2.54) * mm});
            skLineSegment(sketch, "E138.MirrorCS", {"start": v(18.54, 2.54) * mm, "end": v(18.29, 2.1) * mm});
            skLineSegment(sketch, "E139.MirrorCS", {"start": v(21.84, 2.1) * mm, "end": v(21.6, 2.54) * mm});
            skLineSegment(sketch, "E140.MirrorCS", {"start": v(24.13, 2.54) * mm, "end": v(23.88, 2.1) * mm});
            skLineSegment(sketch, "E141.MirrorCS", {"start": v(-23.88, 2.1) * mm, "end": v(-24.13, 2.54) * mm});
            skLineSegment(sketch, "E142.MirrorCS", {"start": v(-10.16, 2.1) * mm, "end": v(-10.41, 2.54) * mm});
            skLineSegment(sketch, "E143.MirrorCS", {"start": v(6.86, 2.54) * mm, "end": v(6.6, 2.1) * mm});
            skLineSegment(sketch, "E144.MirrorCS", {"start": v(11.94, 2.54) * mm, "end": v(11.68, 2.1) * mm});
            skLineSegment(sketch, "E145.MirrorCS", {"start": v(16.51, 2.54) * mm, "end": v(16.26, 2.1) * mm});
            skLineSegment(sketch, "E146.MirrorCS", {"start": v(-18.29, 2.1) * mm, "end": v(-18.54, 2.54) * mm});
            skLineSegment(sketch, "E147.MirrorCS", {"start": v(-16.26, 2.1) * mm, "end": v(-16.5, 2.54) * mm});
            skLineSegment(sketch, "E148.MirrorCS", {"start": v(1.78, 2.54) * mm, "end": v(1.52, 2.1) * mm});
            skLineSegment(sketch, "E149.MirrorCS", {"start": v(8.9, 2.54) * mm, "end": v(8.64, 2.1) * mm});
            skLineSegment(sketch, "E150.MirrorCS", {"start": v(16.26, 2.1) * mm, "end": v(16, 2.54) * mm});
            skLineSegment(sketch, "E151.MirrorCS", {"start": v(-5.59, 2.1) * mm, "end": v(-5.84, 2.54) * mm});
            skLineSegment(sketch, "E152.MirrorCS", {"start": v(3.81, 2.54) * mm, "end": v(3.56, 2.1) * mm});
            skLineSegment(sketch, "E153.MirrorCS", {"start": v(-17.53, 2.54) * mm, "end": v(-17.78, 2.1) * mm});
            skLineSegment(sketch, "E154.MirrorCS", {"start": v(-17.27, 2.1) * mm, "end": v(-17.53, 2.54) * mm});
            skLineSegment(sketch, "E155.MirrorCS", {"start": v(6.1, 2.1) * mm, "end": v(5.84, 2.54) * mm});
            skLineSegment(sketch, "E156.MirrorCS", {"start": v(23.62, 2.54) * mm, "end": v(23.37, 2.1) * mm});
            skLineSegment(sketch, "E157.MirrorCS", {"start": v(17.78, 2.1) * mm, "end": v(17.53, 2.54) * mm});
            skLineSegment(sketch, "E158.MirrorCS", {"start": v(8.38, 2.54) * mm, "end": v(8.13, 2.1) * mm});
            skLineSegment(sketch, "E159.MirrorCS", {"start": v(23.88, 2.1) * mm, "end": v(23.62, 2.54) * mm});
            skLineSegment(sketch, "E160.MirrorCS", {"start": v(9.14, 2.1) * mm, "end": v(8.9, 2.54) * mm});
            skLineSegment(sketch, "E161.MirrorCS", {"start": v(-15.75, 2.1) * mm, "end": v(-16, 2.54) * mm});
            skLineSegment(sketch, "E162.MirrorCS", {"start": v(22.35, 2.1) * mm, "end": v(22.1, 2.54) * mm});
            skLineSegment(sketch, "E163.MirrorCS", {"start": v(20.83, 2.1) * mm, "end": v(20.57, 2.54) * mm});
            skLineSegment(sketch, "E164.MirrorCS", {"start": v(3.05, 2.1) * mm, "end": v(2.8, 2.54) * mm});
            skLineSegment(sketch, "E165.MirrorCS", {"start": v(10.92, 2.54) * mm, "end": v(10.67, 2.1) * mm});
            skLineSegment(sketch, "E166.MirrorCS", {"start": v(19.3, 2.1) * mm, "end": v(19.05, 2.54) * mm});
            skLineSegment(sketch, "E167.MirrorCS", {"start": v(-7.37, 2.54) * mm, "end": v(-7.62, 2.1) * mm});
            skLineSegment(sketch, "E168.MirrorCS", {"start": v(2.8, 2.54) * mm, "end": v(2.54, 2.1) * mm});
            skLineSegment(sketch, "E169.MirrorCS", {"start": v(-10.67, 2.1) * mm, "end": v(-10.92, 2.54) * mm});
            skLineSegment(sketch, "E170.MirrorCS", {"start": v(-1.52, 2.1) * mm, "end": v(-1.78, 2.54) * mm});
            skLineSegment(sketch, "E171.MirrorCS", {"start": v(-11.43, 2.54) * mm, "end": v(-11.68, 2.1) * mm});
            skLineSegment(sketch, "E172.MirrorCS", {"start": v(20.57, 2.54) * mm, "end": v(20.32, 2.1) * mm});
            skLineSegment(sketch, "E173.MirrorCS", {"start": v(-7.11, 2.1) * mm, "end": v(-7.37, 2.54) * mm});
            skLineSegment(sketch, "E174.MirrorCS", {"start": v(5.59, 2.1) * mm, "end": v(5.33, 2.54) * mm});
            skLineSegment(sketch, "E175.MirrorCS", {"start": v(-5.08, 2.1) * mm, "end": v(-5.33, 2.54) * mm});
            skLineSegment(sketch, "E176.MirrorCS", {"start": v(-11.18, 2.1) * mm, "end": v(-11.43, 2.54) * mm});
            skLineSegment(sketch, "E177.MirrorCS", {"start": v(-24.13, 2.54) * mm, "end": v(-24.38, 2.1) * mm});
            skLineSegment(sketch, "E178.MirrorCS", {"start": v(-4.32, 2.54) * mm, "end": v(-4.57, 2.1) * mm});
            skLineSegment(sketch, "E179.MirrorCS", {"start": v(5.33, 2.54) * mm, "end": v(5.08, 2.1) * mm});
            skLineSegment(sketch, "E180.MirrorCS", {"start": v(8.64, 2.1) * mm, "end": v(8.38, 2.54) * mm});
            skLineSegment(sketch, "E181.MirrorCS", {"start": v(11.18, 2.1) * mm, "end": v(10.92, 2.54) * mm});
            skLineSegment(sketch, "E182.MirrorCS", {"start": v(16.76, 2.1) * mm, "end": v(16.51, 2.54) * mm});
            skLineSegment(sketch, "E183.MirrorCS", {"start": v(12.2, 2.1) * mm, "end": v(11.94, 2.54) * mm});
            skLineSegment(sketch, "E184.MirrorCS", {"start": v(-21.84, 2.1) * mm, "end": v(-22.1, 2.54) * mm});
            skLineSegment(sketch, "E185.MirrorCS", {"start": v(19.56, 2.54) * mm, "end": v(19.3, 2.1) * mm});
            skLineSegment(sketch, "E186.MirrorCS", {"start": v(16, 2.54) * mm, "end": v(15.75, 2.1) * mm});
            skLineSegment(sketch, "E187.MirrorCS", {"start": v(4.57, 2.1) * mm, "end": v(4.32, 2.54) * mm});
            skLineSegment(sketch, "E188.MirrorCS", {"start": v(-24.64, 2.8) * mm, "end": v(24.64, 2.8) * mm});
            skLineSegment(sketch, "E189.MirrorCS", {"start": v(19.05, 2.54) * mm, "end": v(18.8, 2.1) * mm});
            skLineSegment(sketch, "E190.MirrorCS", {"start": v(24.64, 2.54) * mm, "end": v(24.38, 2.1) * mm});
            skLineSegment(sketch, "E191.MirrorCS", {"start": v(-22.1, 2.54) * mm, "end": v(-22.35, 2.1) * mm});
            skLineSegment(sketch, "E192.MirrorCS", {"start": v(24.38, 2.1) * mm, "end": v(24.13, 2.54) * mm});
            skLineSegment(sketch, "E193.MirrorCS", {"start": v(11.68, 2.1) * mm, "end": v(11.43, 2.54) * mm});
            skLineSegment(sketch, "E194.MirrorCS", {"start": v(13.97, 2.54) * mm, "end": v(13.72, 2.1) * mm});
            skLineSegment(sketch, "E195.MirrorCS", {"start": v(-6.86, 2.54) * mm, "end": v(-7.11, 2.1) * mm});
            skLineSegment(sketch, "E196.MirrorCS", {"start": v(19.81, 2.1) * mm, "end": v(19.56, 2.54) * mm});
            skLineSegment(sketch, "E197.MirrorCS", {"start": v(18.29, 2.1) * mm, "end": v(18.03, 2.54) * mm});
            skLineSegment(sketch, "E198.MirrorCS", {"start": v(4.83, 2.54) * mm, "end": v(4.57, 2.1) * mm});
            skLineSegment(sketch, "E199.MirrorCS", {"start": v(-23.62, 2.54) * mm, "end": v(-23.88, 2.1) * mm});
            skLineSegment(sketch, "E200.MirrorCS", {"start": v(-18.8, 2.1) * mm, "end": v(-19.05, 2.54) * mm});
            skLineSegment(sketch, "E201.MirrorCS", {"start": v(-13.97, 2.54) * mm, "end": v(-14.22, 2.1) * mm});
            skLineSegment(sketch, "E202.MirrorCS", {"start": v(-3.05, 2.1) * mm, "end": v(-3.3, 2.54) * mm});
            skLineSegment(sketch, "E203.MirrorCS", {"start": v(-9.4, 2.54) * mm, "end": v(-9.65, 2.1) * mm});
            skLineSegment(sketch, "E204.MirrorCS", {"start": v(14.22, 2.1) * mm, "end": v(13.97, 2.54) * mm});
            skLineSegment(sketch, "E205.MirrorCS", {"start": v(5.84, 2.54) * mm, "end": v(5.59, 2.1) * mm});
            skLineSegment(sketch, "E206.MirrorCS", {"start": v(-3.3, 2.54) * mm, "end": v(-3.56, 2.1) * mm});
            skSolve(sketch);
        }
        {
            var Q0;
            Q0=qSketchRegion(id+"F2",true);
            extrude(context, id + "F3", {"entities" : qUnion([Q0]), "operationType" : NewBodyOperationType.REMOVE, "endBound" : BoundingType.SYMMETRIC, "oppositeDirection" : true, "depth" : 25.4 * mm, "offsetDistance" : 25.4 * mm});
        }
        {
            var Q0;
            Q0=makeQuery(id+"F1.opExtrude","CAP_EDGE",EDGE,{"disambiguationData":[OSD([sQuery(id+"F0.wireOp",EDGE,"E0.left")])],"isStart":false});
            var Q1;
            Q1=makeQuery(id+"F1.opExtrude","CAP_EDGE",EDGE,{"disambiguationData":[OSD([sQuery(id+"F0.wireOp",EDGE,"E0.right")])],"isStart":false});
            var Q2;
            Q2=makeQuery(id+"F3.boolean.opBoolean","MERGE",EDGE,{"derivedFrom":[makeQuery(id+"F1.opExtrude","CAP_EDGE",EDGE,{"disambiguationData":[OSD([sQuery(id+"F0.wireOp",EDGE,"E0.top")])],"isStart":false})],"fromTools":[makeQuery(id+"F3.opExtrude","SWEPT_EDGE",EDGE,{"disambiguationData":[OSD([sQuery(id+"F2.wireOp",EDGE,"accb9737-dca4-4821-836c-b98c3f27e90128.MirrorCS"),sQuery(id+"F2.wireOp",EDGE,"accb9737-dca4-4821-836c-b98c3f27e901305.MirrorCS")])]})]});
            var Q3;
            Q3=makeQuery(id+"F3.boolean.opBoolean","MERGE",EDGE,{"derivedFrom":[makeQuery(id+"F1.opExtrude","CAP_EDGE",EDGE,{"disambiguationData":[OSD([sQuery(id+"F0.wireOp",EDGE,"E0.bottom")])],"isStart":false})],"fromTools":[makeQuery(id+"F3.opExtrude","SWEPT_EDGE",EDGE,{"disambiguationData":[OSD([sQuery(id+"F2.wireOp",EDGE,"E4.74.0.1"),sQuery(id+"F2.wireOp",EDGE,"E4.75.0.0")])]})]});
            var Q4;
            Q4=makeQuery(id+"F1.opExtrude","CAP_EDGE",EDGE,{"disambiguationData":[OSD([sQuery(id+"F0.wireOp",EDGE,"E0.right")])],"isStart":true});
            var Q5;
            Q5=makeQuery(id+"F3.boolean.opBoolean","MERGE",EDGE,{"derivedFrom":[makeQuery(id+"F1.opExtrude","CAP_EDGE",EDGE,{"disambiguationData":[OSD([sQuery(id+"F0.wireOp",EDGE,"E0.top")])],"isStart":true})],"fromTools":[makeQuery(id+"F3.opExtrude","SWEPT_EDGE",EDGE,{"disambiguationData":[OSD([sQuery(id+"F2.wireOp",EDGE,"accb9737-dca4-4821-836c-b98c3f27e901234.MirrorCS"),sQuery(id+"F2.wireOp",EDGE,"accb9737-dca4-4821-836c-b98c3f27e901281.MirrorCS")])]})]});
            var Q6;
            Q6=makeQuery(id+"F3.boolean.opBoolean","MERGE",EDGE,{"derivedFrom":[makeQuery(id+"F1.opExtrude","CAP_EDGE",EDGE,{"disambiguationData":[OSD([sQuery(id+"F0.wireOp",EDGE,"E0.bottom")])],"isStart":true})],"fromTools":[makeQuery(id+"F3.opExtrude","SWEPT_EDGE",EDGE,{"disambiguationData":[OSD([sQuery(id+"F2.wireOp",EDGE,"7466ea39-6cbc-46fd-bf35-4a40d964e960.0.75.0"),sQuery(id+"F2.wireOp",EDGE,"7466ea39-6cbc-46fd-bf35-4a40d964e960.3.76.0")])]})]});
            var Q7;
            Q7=makeQuery(id+"F1.opExtrude","CAP_FACE",FACE,{"disambiguationData":[OSD([sQuery(id+"F0.wireOp",EDGE,"E0.bottom"),sQuery(id+"F0.wireOp",EDGE,"E0.top"),sQuery(id+"F0.wireOp",EDGE,"E0.left"),sQuery(id+"F0.wireOp",EDGE,"E0.right")])],"isStart":true});
            fillet(context, id + "F4", {"entities" : qUnion([Q0, Q1, Q2, Q3, Q4, Q5, Q6, Q7]), "radius" : 0.25 * mm, "tangentPropagation" : true, "allowEdgeOverflow" : false});
        }
        {
            var Q0;
            Q0=makeQuery(id+"F1.opExtrude","CAP_FACE",FACE,{"disambiguationData":[OSD([sQuery(id+"F0.wireOp",EDGE,"E0.bottom"),sQuery(id+"F0.wireOp",EDGE,"E0.top"),sQuery(id+"F0.wireOp",EDGE,"E0.left"),sQuery(id+"F0.wireOp",EDGE,"E0.right")])],"isStart":true});
            var sketch = newSketch(context, id + "F5", { "sketchPlane" : qUnion([Q0])});
            skLineSegment(sketch, "E207.bottom", {"start": v(10.16, -0.63) * mm, "end": v(6.99, -0.63) * mm});
            skLineSegment(sketch, "E207.top", {"start": v(10.16, 0.64) * mm, "end": v(6.99, 0.64) * mm});
            skLineSegment(sketch, "E207.left", {"start": v(10.16, -0.63) * mm, "end": v(10.16, 0.64) * mm});
            skLineSegment(sketch, "E207.right", {"start": v(-10.16, -0.64) * mm, "end": v(-10.16, 0.63) * mm});
            skPoint(sketch, "E207.middle", {"position": v(0, 0) * mm});
            skLineSegment(sketch, "E208.bottom", {"start": v(0.64, -2.54) * mm, "end": v(-0.63, -2.54) * mm});
            skLineSegment(sketch, "E208.top", {"start": v(0.63, 2.54) * mm, "end": v(-0.64, 2.54) * mm});
            skLineSegment(sketch, "E208.left", {"start": v(0.64, -2.54) * mm, "end": v(0.64, -0.64) * mm});
            skLineSegment(sketch, "E208.right", {"start": v(-0.63, -2.54) * mm, "end": v(-0.64, -0.64) * mm});
            skLineSegment(sketch, "E209.bottom", {"start": v(-5.72, -2.54) * mm, "end": v(-6.99, -2.54) * mm});
            skLineSegment(sketch, "E209.top", {"start": v(-5.71, 2.54) * mm, "end": v(-6.99, 2.54) * mm});
            skLineSegment(sketch, "E209.left", {"start": v(-5.72, -2.54) * mm, "end": v(-5.72, -0.64) * mm});
            skLineSegment(sketch, "E209.right", {"start": v(-6.99, -2.54) * mm, "end": v(-6.99, -0.64) * mm});
            skPoint(sketch, "E209.middle", {"position": v(-6.35, 0) * mm});
            skLineSegment(sketch, "E210.bottom", {"start": v(6.99, -2.54) * mm, "end": v(5.71, -2.54) * mm});
            skLineSegment(sketch, "E210.top", {"start": v(6.99, 2.54) * mm, "end": v(5.71, 2.54) * mm});
            skLineSegment(sketch, "E210.left", {"start": v(6.98, -2.54) * mm, "end": v(6.99, -0.63) * mm});
            skLineSegment(sketch, "E210.right", {"start": v(5.71, -2.54) * mm, "end": v(5.71, -0.63) * mm});
            skPoint(sketch, "E210.middle", {"position": v(6.35, 0) * mm});
            skLineSegment(sketch, "E211.trimOffspring", {"start": v(-6.99, 0.63) * mm, "end": v(-6.99, 2.54) * mm});
            skLineSegment(sketch, "E212.trimOffspring", {"start": v(-6.99, 0.63) * mm, "end": v(-10.16, 0.63) * mm});
            skLineSegment(sketch, "E213.trimOffspring", {"start": v(-6.99, -0.64) * mm, "end": v(-10.16, -0.64) * mm});
            skLineSegment(sketch, "E214.trimOffspring", {"start": v(-5.72, 0.64) * mm, "end": v(-5.72, 2.54) * mm});
            skLineSegment(sketch, "E215.trimOffspring", {"start": v(-0.64, 0.64) * mm, "end": v(-0.64, 2.54) * mm});
            skLineSegment(sketch, "E216.trimOffspring", {"start": v(-0.64, -0.64) * mm, "end": v(-5.72, -0.64) * mm});
            skLineSegment(sketch, "E217.trimOffspring", {"start": v(-0.64, 0.64) * mm, "end": v(-5.72, 0.64) * mm});
            skLineSegment(sketch, "E218.trimOffspring", {"start": v(0.64, 0.64) * mm, "end": v(0.63, 2.54) * mm});
            skLineSegment(sketch, "E219.trimOffspring", {"start": v(5.71, 0.64) * mm, "end": v(5.71, 2.54) * mm});
            skLineSegment(sketch, "E220.trimOffspring", {"start": v(5.71, 0.64) * mm, "end": v(0.64, 0.64) * mm});
            skLineSegment(sketch, "E221.trimOffspring", {"start": v(6.99, 0.64) * mm, "end": v(6.99, 2.54) * mm});
            skLineSegment(sketch, "E222.trimOffspring", {"start": v(5.71, -0.63) * mm, "end": v(0.64, -0.64) * mm});
            skSolve(sketch);
        }
        {
            var Q0;
            Q0=qSketchRegion(id+"F5",true);
            extrude(context, id + "F6", {"entities" : qUnion([Q0]), "operationType" : NewBodyOperationType.REMOVE, "oppositeDirection" : true, "depth" : 0.5 * mm, "offsetDistance" : 25.4 * mm});
        }
    });
